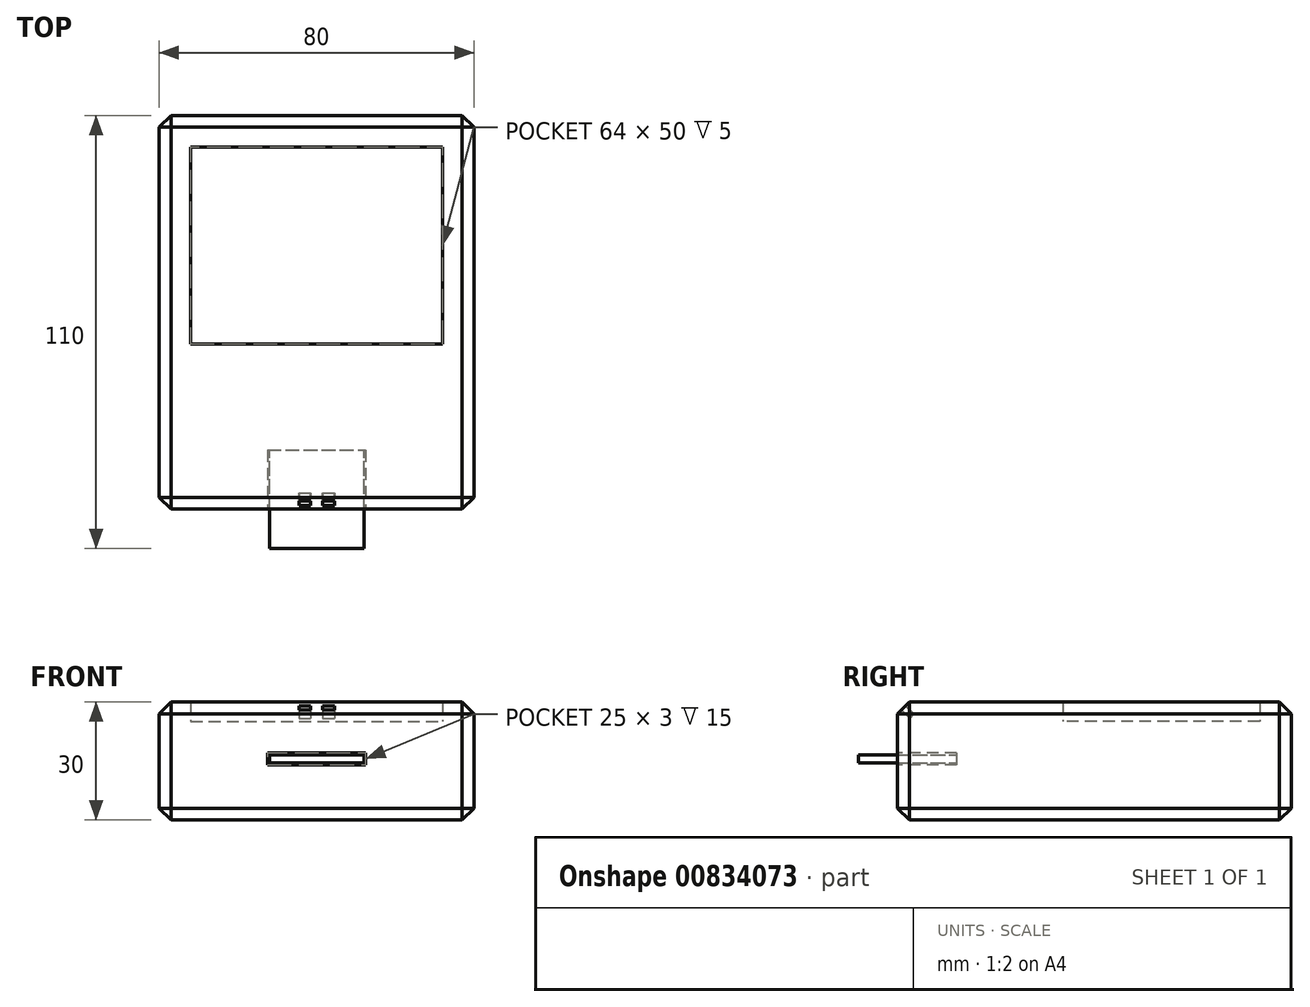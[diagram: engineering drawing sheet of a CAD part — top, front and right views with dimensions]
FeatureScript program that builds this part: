
annotation { "Feature Type Name" : "Feature", "Feature Type Description" : "" }
export const myFeature = defineFeature(function(context is Context, id is Id, definition is map)
    precondition{}
    {
        {
            var Q0;
            Q0=qCreatedBy(makeId("Top.planeOp"),FACE);
            var sketch = newSketch(context, id + "F0", { "sketchPlane" : qUnion([Q0])});
            skLineSegment(sketch, "E0.bottom", {"start": v(0, 0) * mm, "end": v(80, 0) * mm});
            skLineSegment(sketch, "E0.top", {"start": v(0, 100) * mm, "end": v(80, 100) * mm});
            skLineSegment(sketch, "E0.left", {"start": v(0, 0) * mm, "end": v(0, 100) * mm});
            skLineSegment(sketch, "E0.right", {"start": v(80, 0) * mm, "end": v(80, 100) * mm});
            skSolve(sketch);
        }
        {
            var Q0;
            Q0 = qSketchRegion(id + "F0", true);
            extrude(context, id + "F1", {"entities" : qUnion([Q0]), "depth" : 30 * mm, "offsetDistance" : 25 * mm});
        }
        {
            var Q0;
            Q0=makeQuery(id+"F1.opExtrude","CAP_EDGE",EDGE,{"disambiguationData":[OSD([sQuery(id+"F0.wireOp",EDGE,"E0.bottom")])],"isStart":false});
            var Q1;
            Q1=makeQuery(id+"F1.opExtrude","CAP_EDGE",EDGE,{"disambiguationData":[OSD([sQuery(id+"F0.wireOp",EDGE,"E0.right")])],"isStart":false});
            var Q2;
            Q2=makeQuery(id+"F1.opExtrude","SWEPT_EDGE",EDGE,{"disambiguationData":[OSD([sQuery(id+"F0.wireOp",EDGE,"E0.bottom"),sQuery(id+"F0.wireOp",EDGE,"E0.right")])]});
            var Q3;
            Q3=makeQuery(id+"F1.opExtrude","SWEPT_EDGE",EDGE,{"disambiguationData":[OSD([sQuery(id+"F0.wireOp",EDGE,"E0.bottom"),sQuery(id+"F0.wireOp",EDGE,"E0.left")])]});
            var Q4;
            Q4=makeQuery(id+"F1.opExtrude","CAP_EDGE",EDGE,{"disambiguationData":[OSD([sQuery(id+"F0.wireOp",EDGE,"E0.left")])],"isStart":false});
            var Q5;
            Q5=makeQuery(id+"F1.opExtrude","CAP_EDGE",EDGE,{"disambiguationData":[OSD([sQuery(id+"F0.wireOp",EDGE,"E0.top")])],"isStart":false});
            var Q6;
            Q6=makeQuery(id+"F1.opExtrude","SWEPT_EDGE",EDGE,{"disambiguationData":[OSD([sQuery(id+"F0.wireOp",EDGE,"E0.top"),sQuery(id+"F0.wireOp",EDGE,"E0.right")])]});
            var Q7;
            Q7=makeQuery(id+"F1.opExtrude","CAP_EDGE",EDGE,{"disambiguationData":[OSD([sQuery(id+"F0.wireOp",EDGE,"E0.right")])],"isStart":true});
            var Q8;
            Q8=makeQuery(id+"F1.opExtrude","CAP_EDGE",EDGE,{"disambiguationData":[OSD([sQuery(id+"F0.wireOp",EDGE,"E0.bottom")])],"isStart":true});
            var Q9;
            Q9=makeQuery(id+"F1.opExtrude","CAP_EDGE",EDGE,{"disambiguationData":[OSD([sQuery(id+"F0.wireOp",EDGE,"E0.left")])],"isStart":true});
            var Q10;
            Q10=makeQuery(id+"F1.opExtrude","CAP_EDGE",EDGE,{"disambiguationData":[OSD([sQuery(id+"F0.wireOp",EDGE,"E0.top")])],"isStart":true});
            var Q11;
            Q11=makeQuery(id+"F1.opExtrude","SWEPT_FACE",FACE,{"disambiguationData":[OSD([sQuery(id+"F0.wireOp",EDGE,"E0.top")])]});
            chamfer(context, id + "F2", {"entities" : qUnion([Q0, Q1, Q2, Q3, Q4, Q5, Q6, Q7, Q8, Q9, Q10, Q11]), "width" : 3 * mm, "tangentPropagation" : true});
        }
        {
            var Q0;
            Q0=makeQuery(id+"F1.opExtrude","CAP_FACE",FACE,{"disambiguationData":[OSD([sQuery(id+"F0.wireOp",EDGE,"E0.bottom"),sQuery(id+"F0.wireOp",EDGE,"E0.top"),sQuery(id+"F0.wireOp",EDGE,"E0.left"),sQuery(id+"F0.wireOp",EDGE,"E0.right")])],"isStart":false});
            var sketch = newSketch(context, id + "F3", { "sketchPlane" : qUnion([Q0])});
            skLineSegment(sketch, "E1.bottom", {"start": v(8, 92) * mm, "end": v(72, 92) * mm});
            skLineSegment(sketch, "E1.top", {"start": v(8, 42) * mm, "end": v(72, 42) * mm});
            skLineSegment(sketch, "E1.left", {"start": v(8, 92) * mm, "end": v(8, 42) * mm});
            skLineSegment(sketch, "E1.right", {"start": v(72, 92) * mm, "end": v(72, 42) * mm});
            skSolve(sketch);
        }
        {
            var Q0;
            Q0=makeQuery(id+"F3.imprint","IMPRINT",FACE,{"disambiguationData":[TD([[makeQuery(id+"F3.imprint","IMPRINT",EDGE,{"derivedFrom":sQuery(id+"F3.wireOp",EDGE,"E1.bottom")}),-1.0]])]});
            extrude(context, id + "F4", {"entities" : qUnion([Q0]), "operationType" : NewBodyOperationType.REMOVE, "oppositeDirection" : true, "depth" : 5 * mm, "offsetDistance" : 25 * mm});
        }
        {
            var Q0;
            Q0=makeQuery(id+"F1.opExtrude","SWEPT_FACE",FACE,{"disambiguationData":[OSD([sQuery(id+"F0.wireOp",EDGE,"E0.bottom")])]});
            var sketch = newSketch(context, id + "F5", { "sketchPlane" : qUnion([Q0])});
            skLineSegment(sketch, "E2.bottom", {"start": v(27.5, 17) * mm, "end": v(52.5, 17) * mm});
            skLineSegment(sketch, "E2.top", {"start": v(27.5, 14) * mm, "end": v(52.5, 14) * mm});
            skLineSegment(sketch, "E2.left", {"start": v(27.5, 17) * mm, "end": v(27.5, 14) * mm});
            skLineSegment(sketch, "E2.right", {"start": v(52.5, 17) * mm, "end": v(52.5, 14) * mm});
            skLineSegment(sketch, "E3", {"start": v(40, 27) * mm, "end": v(40, 17) * mm, "construction": true});
            skSolve(sketch);
        }
        {
            var Q0;
            Q0=makeQuery(id+"F5.imprint","IMPRINT",FACE,{"disambiguationData":[TD([[makeQuery(id+"F5.imprint","IMPRINT",EDGE,{"derivedFrom":sQuery(id+"F5.wireOp",EDGE,"E2.bottom")}),-1.0]])]});
            extrude(context, id + "F6", {"entities" : qUnion([Q0]), "operationType" : NewBodyOperationType.REMOVE, "oppositeDirection" : true, "depth" : 15 * mm, "offsetDistance" : 25 * mm});
        }
        {
            var Q0;
            {var subQ0=sQuery(id+"F0.wireOp",EDGE,"E0.bottom");Q0=makeQuery(id+"F2.opChamfer","BLEND_FACE",FACE,{"disambiguationData":[OSD([subQ0]),TDD([makeQuery(id+"F1.opExtrude","CAP_EDGE",EDGE,{"disambiguationData":[OSD([subQ0])],"isStart":false})])]});}
            var sketch = newSketch(context, id + "F7", { "sketchPlane" : qUnion([Q0])});
            skLineSegment(sketch, "E4.bottom", {"start": v(35.5, 21.96) * mm, "end": v(38.5, 21.96) * mm});
            skLineSegment(sketch, "E4.top", {"start": v(35.5, 20.46) * mm, "end": v(38.5, 20.46) * mm});
            skLineSegment(sketch, "E4.left", {"start": v(35.5, 21.96) * mm, "end": v(35.5, 20.46) * mm});
            skLineSegment(sketch, "E4.right", {"start": v(38.5, 21.96) * mm, "end": v(38.5, 20.46) * mm});
            skLineSegment(sketch, "E5.1.0.0", {"start": v(41.5, 21.96) * mm, "end": v(44.5, 21.96) * mm});
            skLineSegment(sketch, "E5.1.0.1", {"start": v(41.5, 21.96) * mm, "end": v(41.5, 20.46) * mm});
            skLineSegment(sketch, "E5.1.0.2", {"start": v(41.5, 20.46) * mm, "end": v(44.5, 20.46) * mm});
            skLineSegment(sketch, "E5.1.0.3", {"start": v(44.5, 21.96) * mm, "end": v(44.5, 20.46) * mm});
            skLineSegment(sketch, "E5.direction1", {"start": v(35.5, 21.96) * mm, "end": v(41.5, 21.96) * mm, "construction": true});
            skLineSegment(sketch, "E6", {"start": v(3, 21.21) * mm, "end": v(77, 21.21) * mm, "construction": true});
            skLineSegment(sketch, "E7", {"start": v(38.5, 21.21) * mm, "end": v(41.5, 21.21) * mm, "construction": true});
            skPoint(sketch, "E8", {"position": v(40, 21.21) * mm});
            skSolve(sketch);
        }
        {
            var Q0;
            Q0=makeQuery(id+"F7.imprint","IMPRINT",FACE,{"disambiguationData":[TD([[makeQuery(id+"F7.imprint","IMPRINT",EDGE,{"derivedFrom":sQuery(id+"F7.wireOp",EDGE,"E4.bottom")}),-1.0]])]});
            var Q1;
            Q1=makeQuery(id+"F7.imprint","IMPRINT",FACE,{"disambiguationData":[TD([[makeQuery(id+"F7.imprint","IMPRINT",EDGE,{"derivedFrom":sQuery(id+"F7.wireOp",EDGE,"E5.1.0.0")}),-1.0]])]});
            extrude(context, id + "F8", {"entities" : qUnion([Q0, Q1]), "operationType" : NewBodyOperationType.REMOVE, "oppositeDirection" : true, "depth" : 3 * mm, "offsetDistance" : 25 * mm});
        }
        {
            var Q0;
            Q0=makeQuery(id+"F4.boolean.opBoolean","COPY",FACE,{"derivedFrom":makeQuery(id+"F4.opExtrude","CAP_FACE",FACE,{"disambiguationData":[OSD([sQuery(id+"F3.wireOp",EDGE,"E1.bottom"),sQuery(id+"F3.wireOp",EDGE,"E1.top"),sQuery(id+"F3.wireOp",EDGE,"E1.left"),sQuery(id+"F3.wireOp",EDGE,"E1.right")])],"isStart":false})});
            extrude(context, id + "F9", {"entities" : qUnion([Q0]), "depth" : 5 * mm, "offsetDistance" : 25 * mm});
        }
        {
            var Q0;
            Q0=makeQuery(id+"F8.boolean.opBoolean","COPY",FACE,{"derivedFrom":makeQuery(id+"F8.opExtrude","CAP_FACE",FACE,{"disambiguationData":[OSD([sQuery(id+"F7.wireOp",EDGE,"E4.bottom"),sQuery(id+"F7.wireOp",EDGE,"E4.top"),sQuery(id+"F7.wireOp",EDGE,"E4.left"),sQuery(id+"F7.wireOp",EDGE,"E4.right")])],"isStart":false})});
            var Q1;
            Q1=makeQuery(id+"F8.boolean.opBoolean","COPY",FACE,{"derivedFrom":makeQuery(id+"F8.opExtrude","CAP_FACE",FACE,{"disambiguationData":[OSD([sQuery(id+"F7.wireOp",EDGE,"E5.1.0.0"),sQuery(id+"F7.wireOp",EDGE,"E5.1.0.1"),sQuery(id+"F7.wireOp",EDGE,"E5.1.0.2"),sQuery(id+"F7.wireOp",EDGE,"E5.1.0.3")])],"isStart":false})});
            extrude(context, id + "F10", {"entities" : qUnion([Q0, Q1]), "depth" : 3 * mm, "offsetDistance" : 25 * mm});
        }
        {
            var Q0;
            Q0=makeQuery(id+"F6.boolean.opBoolean","COPY",FACE,{"derivedFrom":makeQuery(id+"F6.opExtrude","CAP_FACE",FACE,{"disambiguationData":[OSD([sQuery(id+"F5.wireOp",EDGE,"E2.bottom"),sQuery(id+"F5.wireOp",EDGE,"E2.top"),sQuery(id+"F5.wireOp",EDGE,"E2.left"),sQuery(id+"F5.wireOp",EDGE,"E2.right")])],"isStart":false})});
            var sketch = newSketch(context, id + "F11", { "sketchPlane" : qUnion([Q0])});
            skLineSegment(sketch, "E9.0", {"start": v(28, 14.5) * mm, "end": v(52, 14.5) * mm});
            skLineSegment(sketch, "E9.1", {"start": v(28, 16.5) * mm, "end": v(28, 14.5) * mm});
            skLineSegment(sketch, "E9.2", {"start": v(28, 16.5) * mm, "end": v(52, 16.5) * mm});
            skLineSegment(sketch, "E9.3", {"start": v(52, 16.5) * mm, "end": v(52, 14.5) * mm});
            skSolve(sketch);
        }
        {
            var Q0;
            Q0=makeQuery(id+"F11.imprint","IMPRINT",FACE,{"disambiguationData":[TD([[makeQuery(id+"F11.imprint","IMPRINT",EDGE,{"derivedFrom":sQuery(id+"F11.wireOp",EDGE,"E9.0")}),1.0]])]});
            extrude(context, id + "F12", {"entities" : qUnion([Q0]), "depth" : 25 * mm, "offsetDistance" : 25 * mm});
        }
    });
